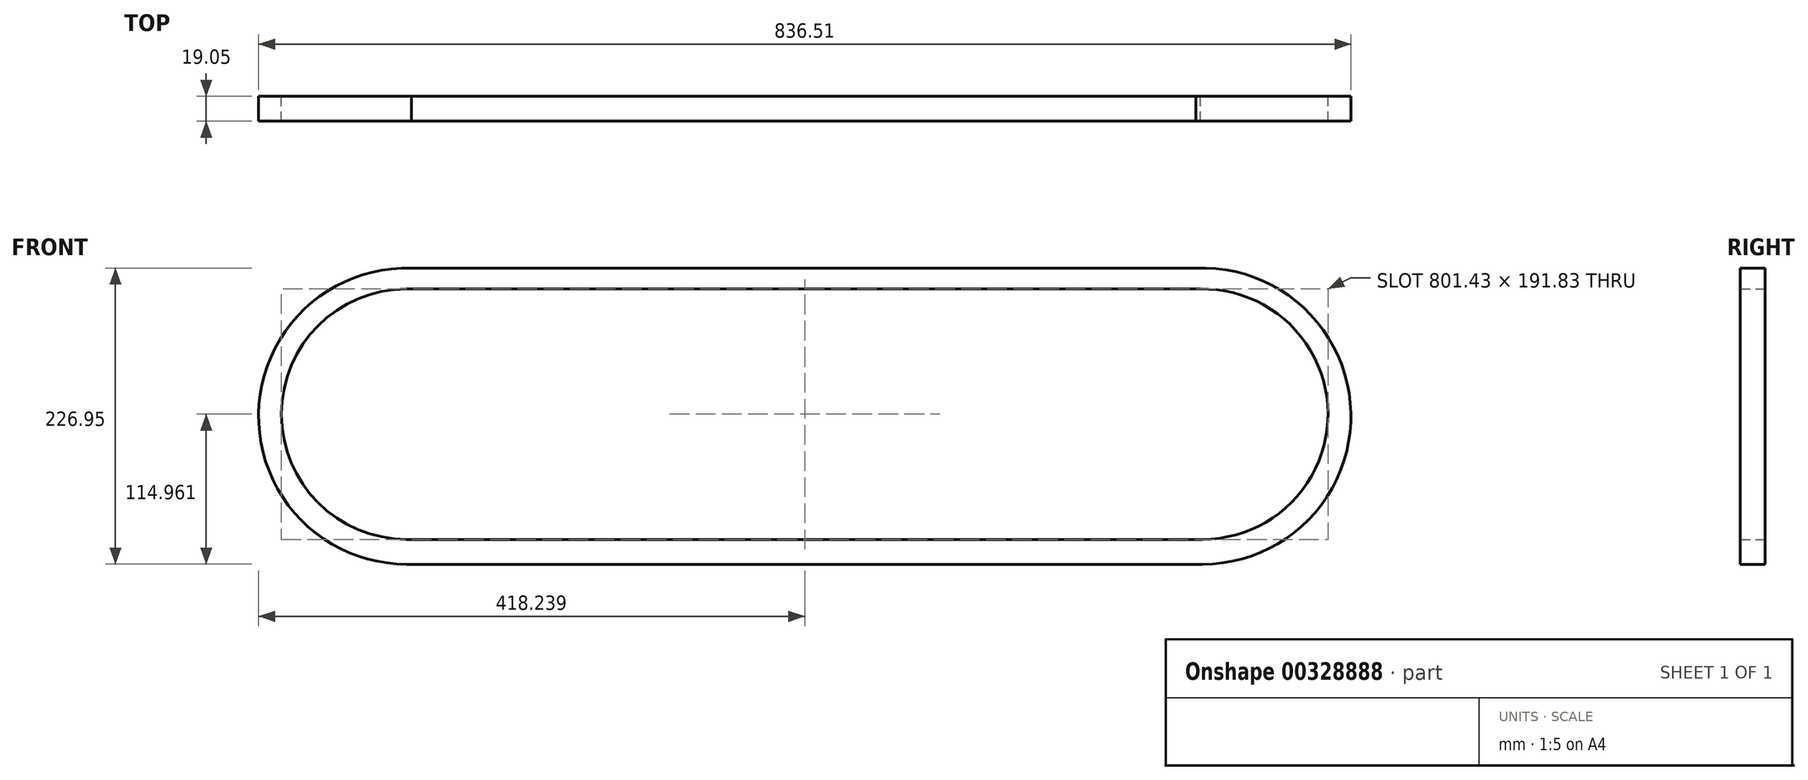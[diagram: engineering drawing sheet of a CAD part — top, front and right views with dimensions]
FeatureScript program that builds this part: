
annotation { "Feature Type Name" : "Feature", "Feature Type Description" : "" }
export const myFeature = defineFeature(function(context is Context, id is Id, definition is map)
    precondition{}
    {
        {
            var Q0;
            Q0=qCreatedBy(makeId("Front.planeOp"),FACE);
            var sketch = newSketch(context, id + "F0", { "sketchPlane" : qUnion([Q0])});
            skLineSegment(sketch, "E0", {"start": v(-301.27, 111.58) * mm, "end": v(299.47, 111.58) * mm});
            skLineSegment(sketch, "E1", {"start": v(-304.81, -115.24) * mm, "end": v(304.79, -115.24) * mm});
            skArc(sketch, "E2", {"start": v(-301.27, 111.58) * mm, "mid": v(-418.24, -0.03) * mm, "end": v(-304.81, -115.24) * mm});
            skArc(sketch, "E3", {"start": v(304.79, -115.24) * mm, "mid": v(418.23, 0.9) * mm, "end": v(299.47, 111.58) * mm});
            skLineSegment(sketch, "E4", {"start": v(-304.81, 95.64) * mm, "end": v(303.01, 95.64) * mm});
            skLineSegment(sketch, "E5", {"start": v(-304.81, -96.2) * mm, "end": v(304.79, -96.2) * mm});
            skArc(sketch, "E6", {"start": v(-304.81, 95.64) * mm, "mid": v(-400.73, -0.28) * mm, "end": v(-304.81, -96.2) * mm});
            skArc(sketch, "E7", {"start": v(304.79, -96.2) * mm, "mid": v(400.7, 0.61) * mm, "end": v(303.01, 95.64) * mm});
            skSolve(sketch);
        }
        {
            var Q0;
            Q0=qSketchRegion(id+"F0",true);
            extrude(context, id + "F1", {"entities" : qUnion([Q0]), "depth" : 19.05 * mm});
        }
    });
